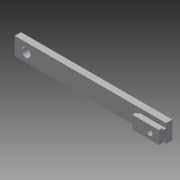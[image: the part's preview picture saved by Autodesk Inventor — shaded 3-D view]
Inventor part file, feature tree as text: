
AUTODESK INVENTOR PART (.ipt)
format: ipt  version: 2013 (Build 170138000, 138)  size: 111,104 bytes
history: native  units: in
note: dims shown in document units (in); Inventor stores cm internally (conversion verified against a paired STEP export)
features: extrude x5, sketch x5
ambient origin geometry x8: Origin, YZ Plane, XZ Plane, XY Plane, X Axis, Y Axis, Z Axis, Center Point
bodies: Solid1 (feature_tree)
feature tree (10):
  extrude  "Extrusion1"  Depth=1.0in
  extrude  "Extrusion2"  Depth=0.25in
  extrude  "Extrusion3"  Depth=0.2in TaperAngle=0.0deg
  extrude  "Extrusion4"  Depth=0.115in
  extrude  "Extrusion5"  Depth=0.35in
  sketch  "Sketch1"  dims[d0=8.5in d1=1.0in]
  sketch  "Sketch2"  dims[d2=0.35in d3=0.0in d4=0.25in]
  sketch  "Sketch3"  dims[d5=1.5in d6=0.2in d7=0.0in]
  sketch  "Sketch4"  dims[d8=0.115in d9=0.115in]
  sketch  "Sketch5"  dims[d10=0.2in d11=0.0in d12=0.35in d14=5.0in d15=0.0in d17=0.5in d18=1.0in d19=0.0in]
